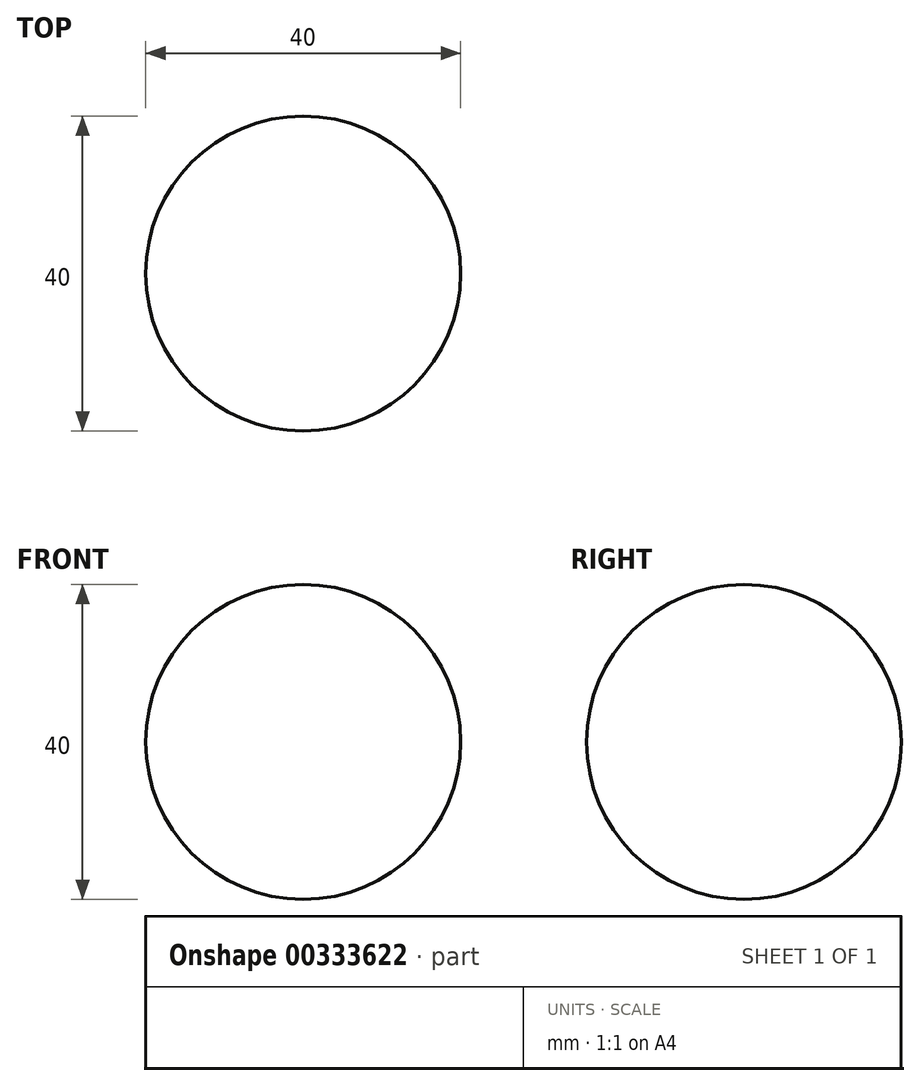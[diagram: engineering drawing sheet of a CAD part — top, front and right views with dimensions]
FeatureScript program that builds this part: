
annotation { "Feature Type Name" : "Feature", "Feature Type Description" : "" }
export const myFeature = defineFeature(function(context is Context, id is Id, definition is map)
    precondition{}
    {
        {
            var Q0;
            Q0=qCreatedBy(makeId("Front.planeOp"),FACE);
            var sketch = newSketch(context, id + "F0", { "sketchPlane" : qUnion([Q0])});
            skLineSegment(sketch, "E0", {"start": v(0, 0) * mm, "end": v(0, 40) * mm});
            skArc(sketch, "E1", {"start": v(0, 40) * mm, "mid": v(-20, 20) * mm, "end": v(0, 0) * mm});
            skSolve(sketch);
        }
        {
            var Q0;
            Q0 = qSketchRegion(id + "F0", true);
            var Q1;
            Q1=sQuery(id+"F0.wireOp",EDGE,"E0");
            revolve(context, id + "F1", {"entities" : qUnion([Q0]), "axis" : qUnion([Q1]), "revolveType" : RevolveType.FULL});
        }
    });
